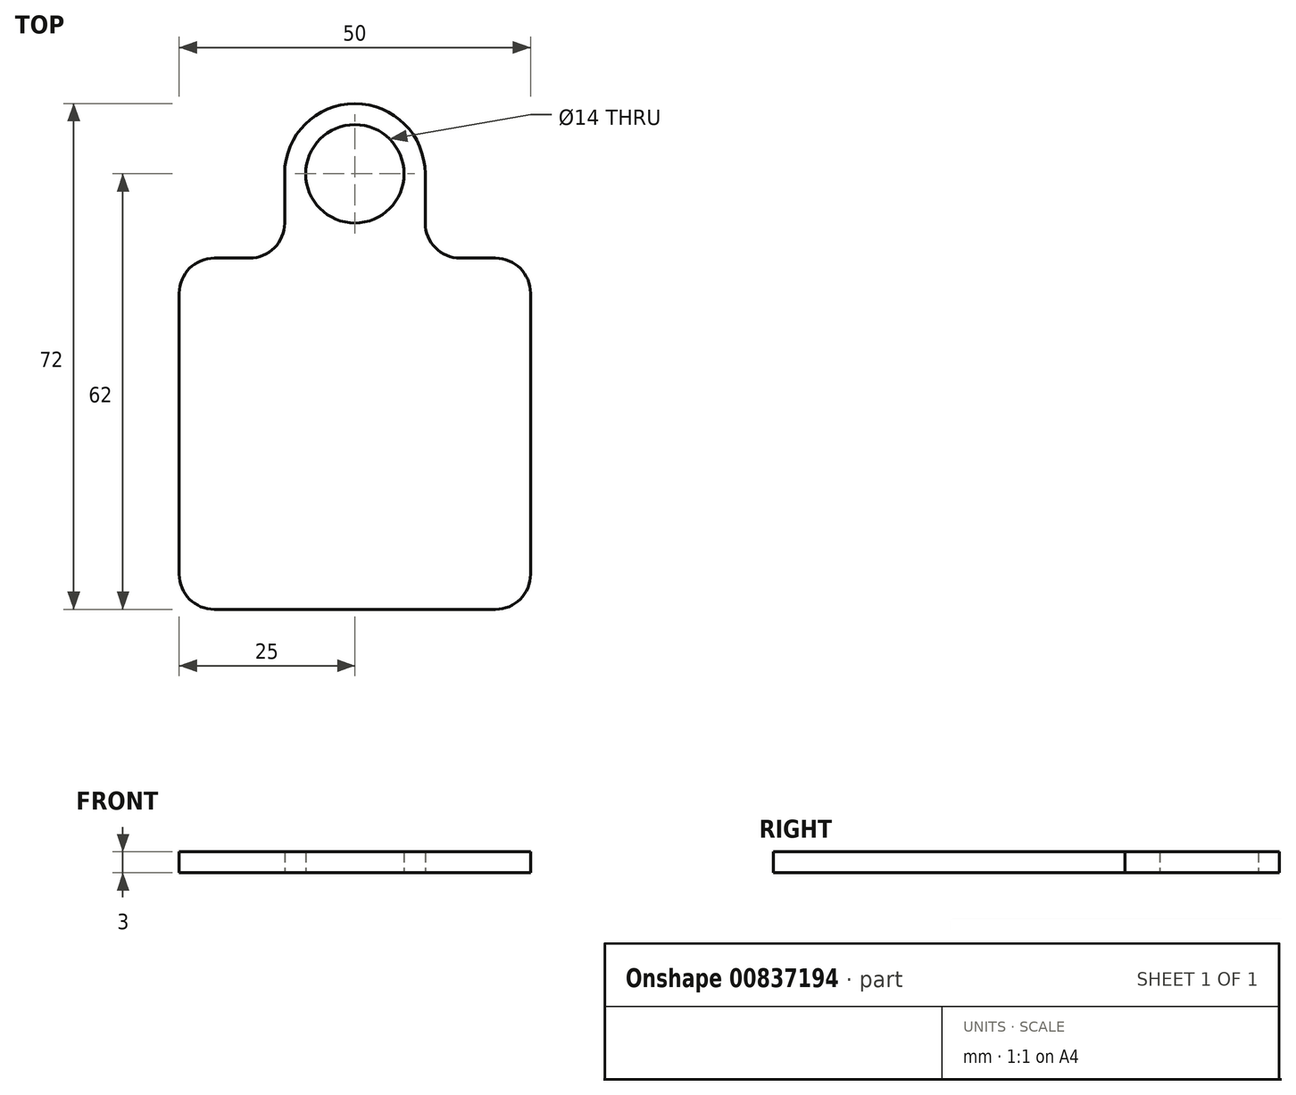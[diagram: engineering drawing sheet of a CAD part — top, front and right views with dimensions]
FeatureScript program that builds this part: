
annotation { "Feature Type Name" : "Feature", "Feature Type Description" : "" }
export const myFeature = defineFeature(function(context is Context, id is Id, definition is map)
    precondition{}
    {
        {
            var Q0;
            Q0=qCreatedBy(makeId("Top.planeOp"),FACE);
            var sketch = newSketch(context, id + "F0", { "sketchPlane" : qUnion([Q0])});
            skLineSegment(sketch, "E0.bottom", {"start": v(20, -25) * mm, "end": v(-20, -25) * mm});
            skLineSegment(sketch, "E0.top", {"start": v(20, 25) * mm, "end": v(15, 25) * mm});
            skLineSegment(sketch, "E0.left", {"start": v(25, -20) * mm, "end": v(25, 20) * mm});
            skLineSegment(sketch, "E0.right", {"start": v(-25, -20) * mm, "end": v(-25, 20) * mm});
            skPoint(sketch, "E0.middle", {"position": v(0, 0) * mm});
            skLineSegment(sketch, "E1", {"start": v(0, 25) * mm, "end": v(0, 37) * mm});
            skArc(sketch, "E2.0.endCap", {"start": v(-10, 37) * mm, "mid": v(0, 47) * mm, "end": v(10, 37) * mm});
            skLineSegment(sketch, "E2.0.left", {"start": v(-10, 30) * mm, "end": v(-10, 37) * mm});
            skLineSegment(sketch, "E2.0.right", {"start": v(10, 30) * mm, "end": v(10, 37) * mm});
            skLineSegment(sketch, "E3.trimOffspring", {"start": v(-15, 25) * mm, "end": v(-20, 25) * mm});
            skCircle(sketch, "E4", {"center": v(0, 37) * mm, "radius": 7 * mm});
            skPoint(sketch, "E5.visualSharp", {"position": v(-25, 25) * mm});
            skArc(sketch, "E5.filletArc", {"start": v(-20, 25) * mm, "mid": v(-23.54, 23.54) * mm, "end": v(-25, 20) * mm});
            skPoint(sketch, "E6.visualSharp", {"position": v(-25, -25) * mm});
            skArc(sketch, "E6.filletArc", {"start": v(-25, -20) * mm, "mid": v(-23.54, -23.54) * mm, "end": v(-20, -25) * mm});
            skPoint(sketch, "E7.visualSharp", {"position": v(25, -25) * mm});
            skArc(sketch, "E7.filletArc", {"start": v(20, -25) * mm, "mid": v(23.54, -23.54) * mm, "end": v(25, -20) * mm});
            skPoint(sketch, "E8.visualSharp", {"position": v(25, 25) * mm});
            skArc(sketch, "E8.filletArc", {"start": v(25, 20) * mm, "mid": v(23.54, 23.54) * mm, "end": v(20, 25) * mm});
            skPoint(sketch, "E9.visualSharp", {"position": v(-10, 25) * mm});
            skArc(sketch, "E9.filletArc", {"start": v(-15, 25) * mm, "mid": v(-11.46, 26.46) * mm, "end": v(-10, 30) * mm});
            skPoint(sketch, "E10.visualSharp", {"position": v(10, 25) * mm});
            skArc(sketch, "E10.filletArc", {"start": v(10, 30) * mm, "mid": v(11.46, 26.46) * mm, "end": v(15, 25) * mm});
            skSolve(sketch);
        }
        {
            var Q0;
            Q0=makeQuery(id+"F0.imprint","IMPRINT",FACE,{"disambiguationData":[TD([[makeQuery(id+"F0.imprint","IMPRINT",EDGE,{"derivedFrom":sQuery(id+"F0.wireOp",EDGE,"E0.bottom")}),-1.0]])]});
            extrude(context, id + "F1", {"entities" : qUnion([Q0]), "depth" : 3 * mm, "offsetDistance" : 25 * mm});
        }
    });
